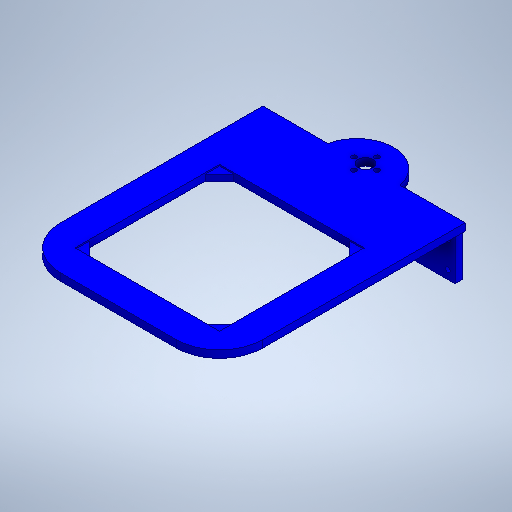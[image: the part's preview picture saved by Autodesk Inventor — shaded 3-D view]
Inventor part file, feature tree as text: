
AUTODESK INVENTOR PART (.ipt)
format: ipt  version: 2025.2 (Build 292293000, 293)  size: 349,184 bytes
history: native  units: mm
features: sketch x4, extrude x4, fillet x2, hole x1
ambient origin geometry x8: Origin, YZ Plane, XZ Plane, XY Plane, X Axis, Y Axis, Z Axis, Center Point
bodies: Body1 (feature_tree)
feature tree (11):
  sketch  "Sketch1"  dims[d0=100.0mm d1=100.0mm]
  extrude  "Extrusion3"  Depth=100.0mm
  extrude  "Extrusion4"  Depth=10.0mm
  fillet  "Fillet1"  Radius=10.0mm
  fillet  "Fillet2"  Radius=20.0mm
  extrude  "Extrusion5"  Depth=140.0mm
  hole  "Hole2"  [1 undecoded]
  extrude  "Extrusion6"  Depth=16.0mm
  sketch  "Sketch2"  dims[d36=150.0mm d37=140.0mm]
  sketch  "Sketch3"  dims[d38=90.0deg d39=50.0mm d40=40.0mm d41=5.0mm d42=0.0mm d43=4.1mm d44=0.0mm d46=30.0mm d47=25.5mm d48=136.0mm d49=34.0mm d50=5.0mm d51=34.0mm d52=5.0mm d53=30.0mm d54=0.0mm d55=5.0mm d56=6.0mm d57=5.0mm d58=6.0mm d59=24.0mm d60=18.0mm d61=24.0mm d62=18.0mm d63=3.4mm d64=6.0mm d65=4.0mm d66=2.0mm d67=90.0deg d68=8.0mm d69=20.594885mm d70=171.0mm d71=10.2mm d72=16.0mm d73=3.5mm d74=40.0mm d76=360.0deg d78=0.0mm d79=0.0mm]
  sketch  "Sketch Circular Pattern1"  dims[d14=10.0mm d15=10.0mm d16=10.0mm d35=20.0mm]
note: 1 required parameter value undecoded (feature->parameter linkage not recoverable at this tier; creation-order binding heuristic only, values carry confidence <= 0.55)
